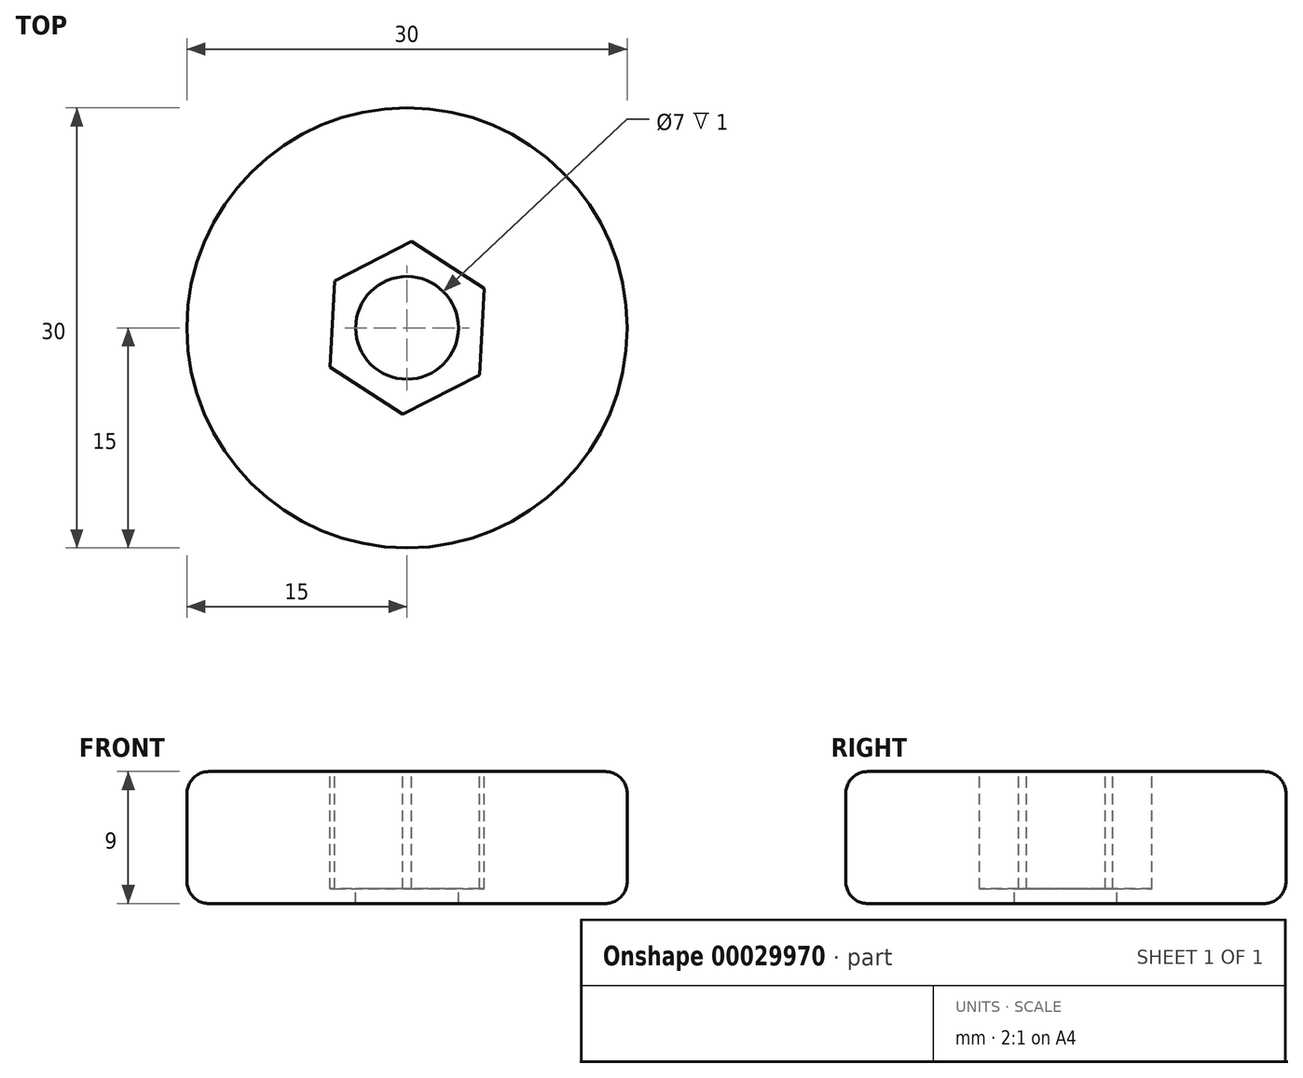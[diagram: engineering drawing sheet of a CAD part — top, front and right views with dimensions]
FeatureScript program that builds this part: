
annotation { "Feature Type Name" : "Feature", "Feature Type Description" : "" }
export const myFeature = defineFeature(function(context is Context, id is Id, definition is map)
    precondition{}
    {
        {
            var Q0;
            Q0=qCreatedBy(makeId("Top.planeOp"),FACE);
            var sketch = newSketch(context, id + "F0", { "sketchPlane" : qUnion([Q0])});
            skCircle(sketch, "E0", {"center": v(0, 0) * mm, "radius": 15 * mm});
            skSolve(sketch);
        }
        {
            var Q0;
            Q0 = qSketchRegion(id + "F0", true);
            extrude(context, id + "F1", {"entities" : qUnion([Q0]), "depth" : 9 * mm});
        }
        {
            var Q0;
            Q0=makeQuery(id+"F1.opExtrude","CAP_FACE",FACE,{"disambiguationData":[OSD([sQuery(id+"F0.wireOp",EDGE,"E0")])],"isStart":false});
            var sketch = newSketch(context, id + "F2", { "sketchPlane" : qUnion([Q0])});
            skCircle(sketch, "E1.cCircle", {"center": v(0, 0) * mm, "radius": 5.1 * mm, "construction": true});
            skLineSegment(sketch, "E1.0", {"start": v(4.94, -3.2) * mm, "end": v(-0.3, -5.88) * mm});
            skLineSegment(sketch, "E1.1", {"start": v(-0.3, -5.88) * mm, "end": v(-5.25, -2.68) * mm});
            skLineSegment(sketch, "E1.2", {"start": v(-5.25, -2.68) * mm, "end": v(-4.94, 3.2) * mm});
            skLineSegment(sketch, "E1.3", {"start": v(-4.94, 3.2) * mm, "end": v(0.3, 5.88) * mm});
            skLineSegment(sketch, "E1.4", {"start": v(0.3, 5.88) * mm, "end": v(5.25, 2.68) * mm});
            skLineSegment(sketch, "E1.5", {"start": v(5.25, 2.68) * mm, "end": v(4.94, -3.2) * mm});
            skPoint(sketch, "E1.0.midPoint", {"position": v(2.32, -4.54) * mm});
            skSolve(sketch);
        }
        {
            var Q0;
            Q0 = qSketchRegion(id + "F2", true);
            extrude(context, id + "F3", {"entities" : qUnion([Q0]), "operationType" : NewBodyOperationType.REMOVE, "oppositeDirection" : true, "depth" : 8 * mm});
        }
        {
            var Q0;
            Q0=makeQuery(id+"F1.opExtrude","CAP_EDGE",EDGE,{"disambiguationData":[OSD([sQuery(id+"F0.wireOp",EDGE,"E0")])],"isStart":false});
            fillet(context, id + "F4", {"entities" : qUnion([Q0]), "radius" : 1.5 * mm, "tangentPropagation" : true, "allowEdgeOverflow" : false});
        }
        {
            var Q0;
            Q0=makeQuery(id+"F1.opExtrude","CAP_EDGE",EDGE,{"disambiguationData":[OSD([sQuery(id+"F0.wireOp",EDGE,"E0")])],"isStart":true});
            fillet(context, id + "F5", {"entities" : qUnion([Q0]), "radius" : 1.5 * mm, "tangentPropagation" : true, "allowEdgeOverflow" : false});
        }
        {
            var Q0;
            Q0=makeQuery(id+"F3.boolean.opBoolean","COPY",FACE,{"derivedFrom":makeQuery(id+"F3.opExtrude","CAP_FACE",FACE,{"disambiguationData":[OSD([sQuery(id+"F2.wireOp",EDGE,"E1.0"),sQuery(id+"F2.wireOp",EDGE,"E1.1"),sQuery(id+"F2.wireOp",EDGE,"E1.2"),sQuery(id+"F2.wireOp",EDGE,"E1.3"),sQuery(id+"F2.wireOp",EDGE,"E1.4"),sQuery(id+"F2.wireOp",EDGE,"E1.5")])],"isStart":false})});
            var sketch = newSketch(context, id + "F6", { "sketchPlane" : qUnion([Q0])});
            skCircle(sketch, "E2", {"center": v(0, 0) * mm, "radius": 3.5 * mm});
            skSolve(sketch);
        }
        {
            var Q0;
            Q0 = qSketchRegion(id + "F6", true);
            extrude(context, id + "F7", {"entities" : qUnion([Q0]), "operationType" : NewBodyOperationType.REMOVE, "endBound" : BoundingType.THROUGH_ALL, "oppositeDirection" : true, "depth" : 25 * mm});
        }
    });
